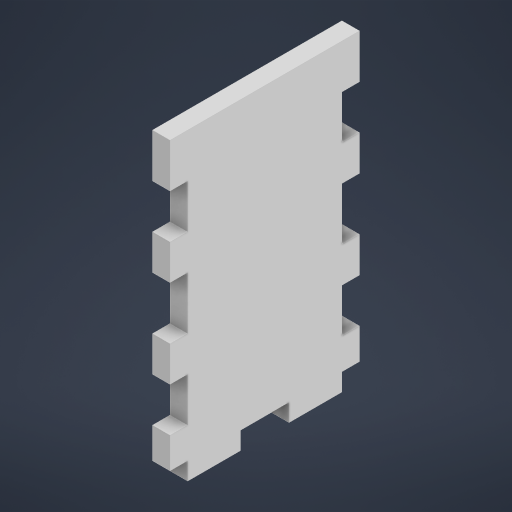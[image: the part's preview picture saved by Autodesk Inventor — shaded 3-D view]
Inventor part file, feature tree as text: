
AUTODESK INVENTOR PART (.ipt)
format: ipt  version: 2023.2 (Build 272271000, 271)  size: 266,752 bytes
history: native  units: mm
features: sketch x1
ambient origin geometry x8: Origin, YZ Plane, XZ Plane, XY Plane, X Axis, Y Axis, Z Axis, Center Point
bodies: Body1 (feature_tree)
feature tree (1):
  sketch  "Sketch1"  dims[d228=69.0mm d229=43.0mm d230=4.0mm d231=0.0mm d246=12.0mm d248=10.0mm d250=8.0mm d251=4.0mm d252=0.0mm d253=4.0mm d254=12.0mm d255=12.0mm d256=10.0mm d9=0.5mm d10=0.872665mm d11=0.5mm d12=0.872665mm d13=0.5mm d14=0.872665mm d27=0.5mm d28=0.872665mm d29=0.5mm d30=0.872665mm d88=0.5mm d89=0.872665mm d90=0.5mm d91=0.872665mm d116=0.5mm d117=0.872665mm d118=0.5mm d119=0.872665mm d154=0.5mm d155=0.872665mm d156=0.5mm d157=0.872665mm d181=0.5mm d182=0.872665mm d183=0.5mm d184=0.872665mm d221=0.5mm d222=0.872665mm d223=0.5mm d224=0.872665mm]
